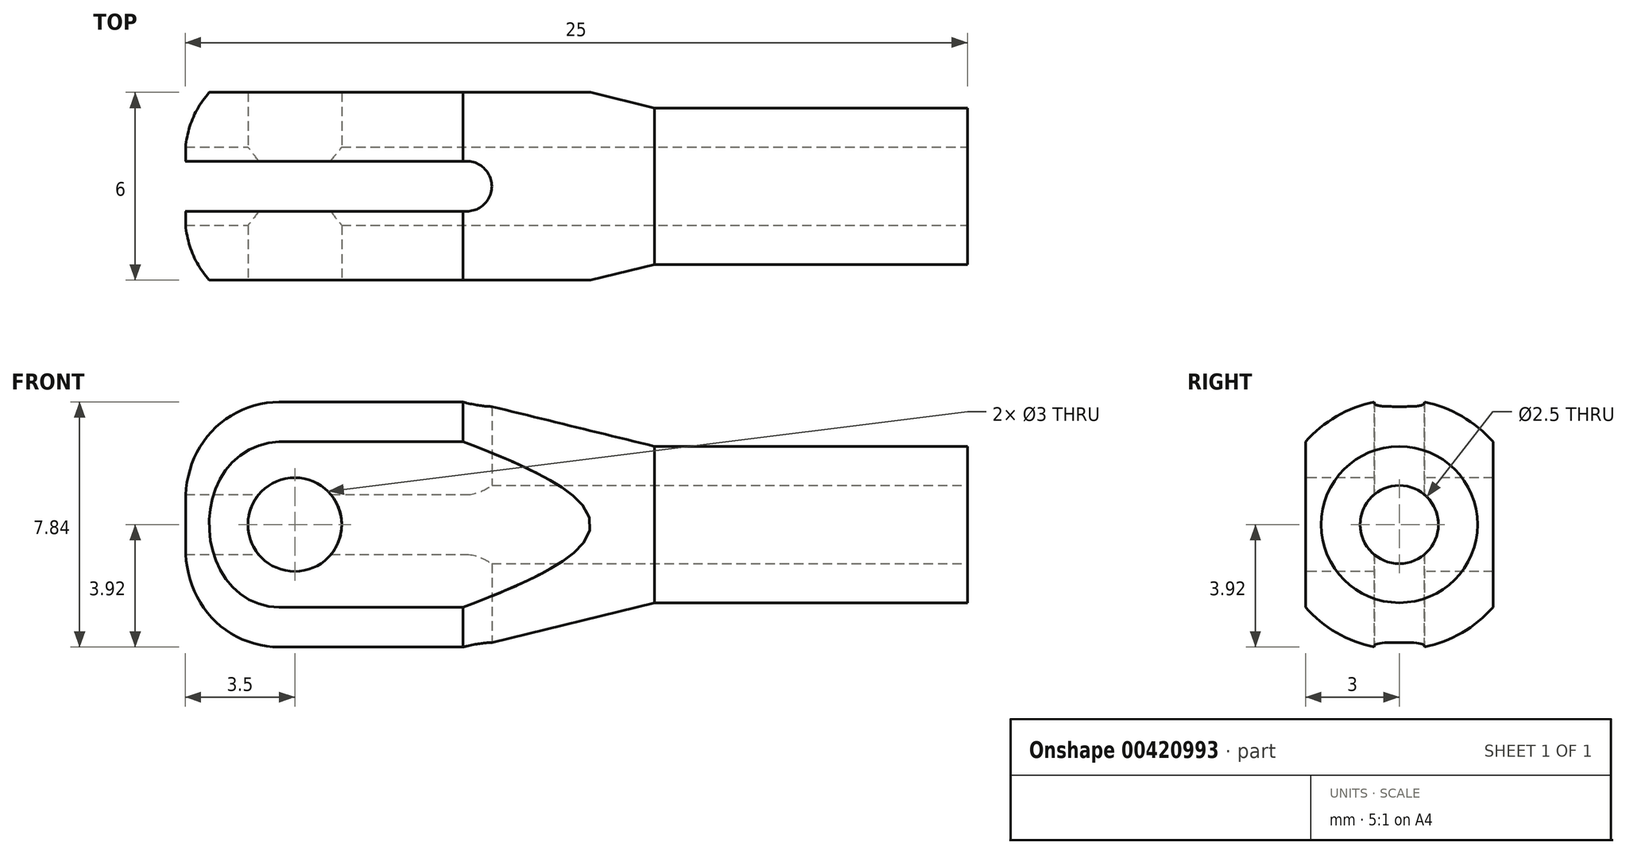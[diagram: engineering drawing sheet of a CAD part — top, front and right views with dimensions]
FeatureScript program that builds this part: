
annotation { "Feature Type Name" : "Feature", "Feature Type Description" : "" }
export const myFeature = defineFeature(function(context is Context, id is Id, definition is map)
    precondition{}
    {
        {
            var Q0;
            Q0=qCreatedBy(makeId("Top.planeOp"),FACE);
            var sketch = newSketch(context, id + "F0", { "sketchPlane" : qUnion([Q0])});
            skLineSegment(sketch, "E0", {"start": v(0, 0) * mm, "end": v(25, 0) * mm, "construction": true});
            skLineSegment(sketch, "E1", {"start": v(25, 0) * mm, "end": v(25, 2.5) * mm});
            skLineSegment(sketch, "E2", {"start": v(25, 2.5) * mm, "end": v(15, 2.5) * mm});
            skLineSegment(sketch, "E3", {"start": v(15, 2.5) * mm, "end": v(8.87, 4) * mm});
            skLineSegment(sketch, "E4", {"start": v(8.87, 4) * mm, "end": v(3, 4) * mm});
            skLineSegment(sketch, "E5", {"start": v(0, 1) * mm, "end": v(0, 0) * mm});
            skLineSegment(sketch, "E6", {"start": v(0, 0) * mm, "end": v(25, 0) * mm});
            skPoint(sketch, "E7.visualSharp", {"position": v(0, 4) * mm});
            skArc(sketch, "E7.filletArc", {"start": v(3, 4) * mm, "mid": v(0.88, 3.12) * mm, "end": v(0, 1) * mm});
            skSolve(sketch);
        }
        {
            var Q0;
            Q0=makeQuery(id+"F0.imprint","IMPRINT",FACE,{"disambiguationData":[TD([[makeQuery(id+"F0.imprint","IMPRINT",EDGE,{"derivedFrom":sQuery(id+"F0.wireOp",EDGE,"E1")}),1.0]])]});
            var Q1;
            Q1=sQuery(id+"F0.wireOp",EDGE,"E6");
            revolve(context, id + "F1", {"entities" : qUnion([Q0]), "axis" : qUnion([Q1]), "revolveType" : RevolveType.FULL});
        }
        {
            var Q0;
            Q0=qCreatedBy(makeId("Front.planeOp"),FACE);
            cPlane(context, id + "F2", {"entities" : qUnion([Q0]), "cplaneType" : CPlaneType.OFFSET, "offset" : 3 * mm, "oppositeDirection" : true, "width" : 150 * mm, "height" : 150 * mm});
        }
        {
            var Q0;
            Q0=qCreatedBy(id+"F2.planeOp",FACE);
            var sketch = newSketch(context, id + "F3", { "sketchPlane" : qUnion([Q0])});
            skLineSegment(sketch, "E8.bottom", {"start": v(13.92, 6.5) * mm, "end": v(-1.65, 6.5) * mm});
            skLineSegment(sketch, "E8.top", {"start": v(13.92, -5.25) * mm, "end": v(-1.65, -5.25) * mm});
            skLineSegment(sketch, "E8.left", {"start": v(13.92, 6.5) * mm, "end": v(13.92, -5.25) * mm});
            skLineSegment(sketch, "E8.right", {"start": v(-1.65, 6.5) * mm, "end": v(-1.65, -5.25) * mm});
            skSolve(sketch);
        }
        {
            var Q0;
            Q0 = qSketchRegion(id + "F3", true);
            extrude(context, id + "F4", {"entities" : qUnion([Q0]), "operationType" : NewBodyOperationType.REMOVE, "oppositeDirection" : true, "depth" : 2.2 * mm});
        }
        {
            var Q0;
            Q0=qCreatedBy(makeId("Front.planeOp"),FACE);
            cPlane(context, id + "F5", {"entities" : qUnion([Q0]), "cplaneType" : CPlaneType.OFFSET, "offset" : 3 * mm, "width" : 150 * mm, "height" : 150 * mm});
        }
        {
            var Q0;
            Q0=qCreatedBy(id+"F5.planeOp",FACE);
            var sketch = newSketch(context, id + "F6", { "sketchPlane" : qUnion([Q0])});
            skLineSegment(sketch, "E9.bottom", {"start": v(0, 4.57) * mm, "end": v(15.33, 4.57) * mm});
            skLineSegment(sketch, "E9.top", {"start": v(0, -4.85) * mm, "end": v(15.33, -4.85) * mm});
            skLineSegment(sketch, "E9.left", {"start": v(0, 4.57) * mm, "end": v(0, -4.85) * mm});
            skLineSegment(sketch, "E9.right", {"start": v(15.33, 4.57) * mm, "end": v(15.33, -4.85) * mm});
            skSolve(sketch);
        }
        {
            var Q0;
            Q0 = qSketchRegion(id + "F6", true);
            extrude(context, id + "F7", {"entities" : qUnion([Q0]), "operationType" : NewBodyOperationType.REMOVE, "depth" : 5.1 * mm});
        }
        {
            var Q0;
            Q0=makeQuery(id+"F7.boolean.opBoolean","COPY",FACE,{"derivedFrom":makeQuery(id+"F7.opExtrude","CAP_FACE",FACE,{"disambiguationData":[OSD([sQuery(id+"F6.wireOp",EDGE,"E9.bottom"),sQuery(id+"F6.wireOp",EDGE,"E9.top"),sQuery(id+"F6.wireOp",EDGE,"E9.left"),sQuery(id+"F6.wireOp",EDGE,"E9.right")])],"isStart":true})});
            var sketch = newSketch(context, id + "F8", { "sketchPlane" : qUnion([Q0])});
            skLineSegment(sketch, "E10", {"start": v(0, 0) * mm, "end": v(3.5, 0) * mm, "construction": true});
            skCircle(sketch, "E11", {"center": v(3.5, 0) * mm, "radius": 1.5 * mm});
            skSolve(sketch);
        }
        {
            var Q0;
            Q0 = qSketchRegion(id + "F8", true);
            extrude(context, id + "F9", {"entities" : qUnion([Q0]), "operationType" : NewBodyOperationType.REMOVE, "oppositeDirection" : true, "depth" : 16.2 * mm});
        }
        {
            var Q0;
            Q0=qCreatedBy(makeId("Top.planeOp"),FACE);
            var sketch = newSketch(context, id + "F10", { "sketchPlane" : qUnion([Q0])});
            skLineSegment(sketch, "E12.top", {"start": v(0, 0.8) * mm, "end": v(9, 0.8) * mm});
            skLineSegment(sketch, "E12.left", {"start": v(0, 0) * mm, "end": v(0, 0.8) * mm});
            skLineSegment(sketch, "E13.top", {"start": v(0, -0.8) * mm, "end": v(9, -0.8) * mm});
            skLineSegment(sketch, "E13.left", {"start": v(0, 0) * mm, "end": v(0, -0.8) * mm});
            skArc(sketch, "E14", {"start": v(9, -0.8) * mm, "mid": v(9.8, 0) * mm, "end": v(9, 0.8) * mm});
            skSolve(sketch);
        }
        {
            var Q0;
            Q0 = qSketchRegion(id + "F10", true);
            extrude(context, id + "F11", {"entities" : qUnion([Q0]), "operationType" : NewBodyOperationType.REMOVE, "endBound" : BoundingType.SYMMETRIC, "depth" : 25 * mm});
        }
        {
            var Q0;
            Q0=makeQuery(id+"F1.opRevolve","SWEPT_FACE",FACE,{"disambiguationData":[OSD([sQuery(id+"F0.wireOp",EDGE,"E1")])]});
            var sketch = newSketch(context, id + "F12", { "sketchPlane" : qUnion([Q0])});
            skCircle(sketch, "E15", {"center": v(0, 0) * mm, "radius": 1.25 * mm});
            skSolve(sketch);
        }
        {
            var Q0;
            Q0 = qSketchRegion(id + "F12", true);
            extrude(context, id + "F13", {"entities" : qUnion([Q0]), "operationType" : NewBodyOperationType.REMOVE, "oppositeDirection" : true, "depth" : 25 * mm});
        }
    });
